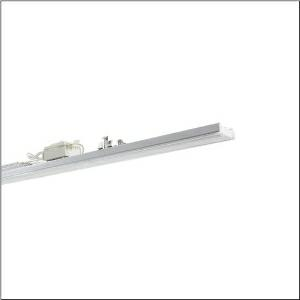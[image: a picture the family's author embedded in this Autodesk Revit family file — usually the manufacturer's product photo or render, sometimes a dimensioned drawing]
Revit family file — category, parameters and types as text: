
# Revit family: licross_11_recessed_mo_51tl12dv4fxg
name_source: partatom
category: Lighting Fixtures
units: mm (PartAtom-declared; Revit-internal decimal feet)

## family parameters
Cut with Voids When Loaded = No
Host = Face
Light Source = No
Part Type = Normal
Room Calculation Point = No
Round Connector Dimension = Use Diameter
Shared = No

## types (1)
- --- (1 x LED, 15360 lm, 84.1 W, 4000K)
    Apparent Load = 84 VA
    CIE Flux Codes = 67 92 99 100 100
    Color Rendering = 80
    Color Temperature = 4000K
    Default Elevation = 1800 mm
    Description = Licross 11 Recessed MO, luminaire insert, of sheet steel, coil coated, white, length: 2.250mm, width: 66mm, height: 67mm, LED rated luminous flux: 15.360lm, light colour: 840, SDCM (Standard Deviation of Colour Matching)MacAdam ≤ 2 SDCM (initial), control gear: DALI 2, with plug, 5-pole, with phase selection, mains connection: 220..240V, AC, 50/60Hz, rated input power: 84W, internal wiring halogen-free, primary optical cover: cover, of PMMA, light emission: direct distribution, primary light characteristic: symmetric, protection rating (complete): IP40, insulation class (complete): insulation class I (protective earthing), certification: CE, ENEC, VDE, UKCA, protection symbol: D if used in an environment without relevant dust loads with corresponding accessories, impact resistance: IK06, permissible ambient temperature for indoor applications: -25..+35°C, corresponds to IFS (International Featured Standards) requirements for safety and quality in the food industry, reducing of maximum allowable ambient temperature of 5°C with ceiling mounting, LABS conformity tested according to VDMA 24364:2018-05, The light source and the operating device comply with the requirements of the Ecodesign Regulation (EU) 2019/2020 and are replaceable in accordance with this regulation, packaging unit: 1 piece
    Height = 58 mm
    Lamp = 1 x LED
    Lamp Light Flux = 15360 lm
    Lamp Power = 84.1 W
    Lamp count = 1
    Length = 2250 mm
    Luminous efficacy = 183 lm/W
    Manufacturer = Siteco
    ModVariant = No
    Model = 51TL12DV4FXG
    Mounting Place = Ceiling
    Mounting Type = Pendant
    Number of Poles = 1
    OnlyDefault = Yes
    Power Factor = 1
    Product Name = Licross 11 Recessed MO
    Product group = luminaire insert | ceiling pendant
    ProductGroupID = 901
    Protection Class = Protection class I
    Protection Degree = IP 40
    RLX_Detail_Level = 1
    RLX_Emergency_Light_Flux = 0 lm
    RLX_Emergency_Type = 0
    RLX_Emergency_Type_DB = No
    RlxData = <blob elided: 29713 chars, md5=fa9f48e4>
    Socket = socket
    Standby Power = 0 W
    System Light Flux = 15360 lm
    System Power = 84 W
    Type Comments = factory setting: luminous flux: 100 % | dim-lin: 254 | 378 mA
    Type Image = l_1296930.jpg
    URL = http://relux.com
    VarID = @adj_101973
    Voltage = 0 V
    Weight = 0.00 kg
    Width = 66 mm

## geometry (parser evidence)
native form markers: Blend x4, Sweep x10
no freeform markers — native parametric forms only
